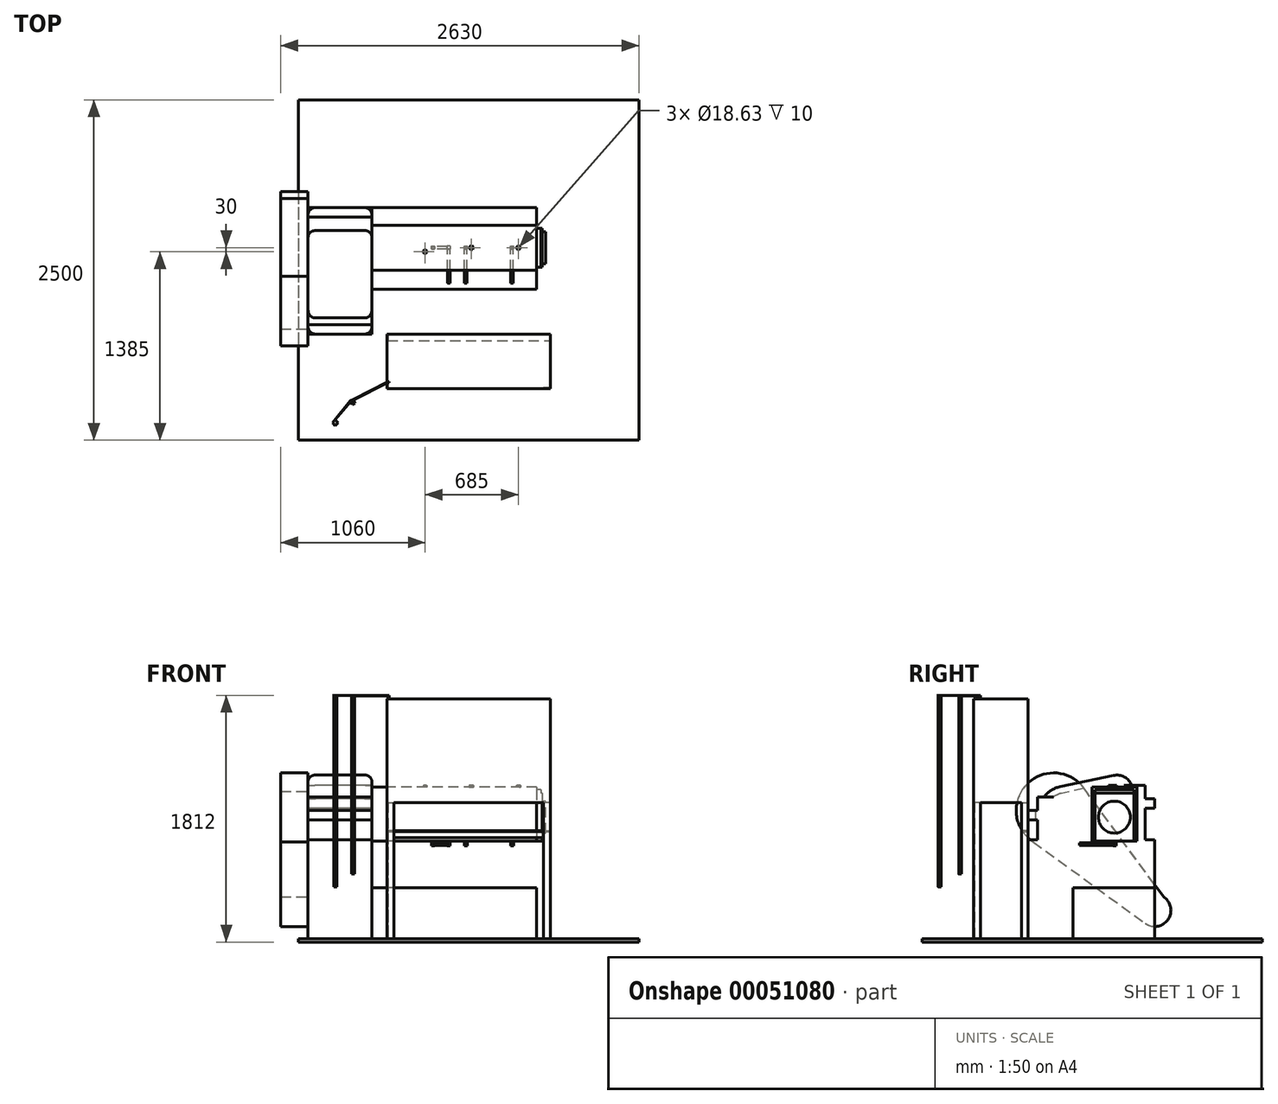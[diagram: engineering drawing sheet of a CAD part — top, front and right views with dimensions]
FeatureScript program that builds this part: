
annotation { "Feature Type Name" : "Feature", "Feature Type Description" : "" }
export const myFeature = defineFeature(function(context is Context, id is Id, definition is map)
    precondition{}
    {
        {
            var Q0;
            Q0=qCreatedBy(makeId("Top.planeOp"),FACE);
            var sketch = newSketch(context, id + "F0", { "sketchPlane" : qUnion([Q0])});
            skLineSegment(sketch, "E0.bottom", {"start": v(-1250, 1250) * mm, "end": v(1250, 1250) * mm});
            skLineSegment(sketch, "E0.top", {"start": v(-1250, -1250) * mm, "end": v(1250, -1250) * mm});
            skLineSegment(sketch, "E0.left", {"start": v(-1250, 1250) * mm, "end": v(-1250, -1250) * mm});
            skLineSegment(sketch, "E0.right", {"start": v(1250, 1250) * mm, "end": v(1250, -1250) * mm});
            skSolve(sketch);
        }
        {
            var Q0;
            Q0=qSketchRegion(id+"F0",true);
            extrude(context, id + "F1", {"entities" : qUnion([Q0]), "depth" : 25 * mm});
        }
        {
            var Q0;
            Q0=makeQuery(id+"F1.opExtrude","CAP_FACE",FACE,{"disambiguationData":[OSD([sQuery(id+"F0.wireOp",EDGE,"E0.bottom"),sQuery(id+"F0.wireOp",EDGE,"E0.top"),sQuery(id+"F0.wireOp",EDGE,"E0.left"),sQuery(id+"F0.wireOp",EDGE,"E0.right")])],"isStart":false});
            var sketch = newSketch(context, id + "F2", { "sketchPlane" : qUnion([Q0])});
            skLineSegment(sketch, "E1", {"start": v(-595, -520) * mm, "end": v(-595, -475) * mm});
            skLineSegment(sketch, "E2", {"start": v(-595, -475) * mm, "end": v(-550, -475) * mm});
            skLineSegment(sketch, "E3", {"start": v(-550, -475) * mm, "end": v(-550, -470) * mm});
            skLineSegment(sketch, "E4", {"start": v(-550, -470) * mm, "end": v(-600, -470) * mm});
            skLineSegment(sketch, "E5", {"start": v(-600, -470) * mm, "end": v(-600, -520) * mm});
            skLineSegment(sketch, "E6", {"start": v(-600, -520) * mm, "end": v(-595, -520) * mm});
            skLineSegment(sketch, "E7.MirrorCS", {"start": v(600, -520) * mm, "end": v(595, -520) * mm});
            skLineSegment(sketch, "E8.MirrorCS", {"start": v(550, -475) * mm, "end": v(550, -470) * mm});
            skLineSegment(sketch, "E9.MirrorCS", {"start": v(600, -470) * mm, "end": v(600, -520) * mm});
            skLineSegment(sketch, "E10.MirrorCS", {"start": v(550, -470) * mm, "end": v(600, -470) * mm});
            skLineSegment(sketch, "E11.MirrorCS", {"start": v(595, -475) * mm, "end": v(550, -475) * mm});
            skLineSegment(sketch, "E12.MirrorCS", {"start": v(595, -520) * mm, "end": v(595, -475) * mm});
            skLineSegment(sketch, "E13", {"start": v(-600, -820) * mm, "end": v(-595, -820) * mm});
            skLineSegment(sketch, "E14", {"start": v(-595, -820) * mm, "end": v(-595, -865) * mm});
            skLineSegment(sketch, "E15", {"start": v(-595, -865) * mm, "end": v(-550, -865) * mm});
            skLineSegment(sketch, "E16", {"start": v(-550, -865) * mm, "end": v(-550, -870) * mm});
            skLineSegment(sketch, "E17", {"start": v(-550, -870) * mm, "end": v(-600, -870) * mm});
            skLineSegment(sketch, "E18", {"start": v(-600, -870) * mm, "end": v(-600, -820) * mm});
            skLineSegment(sketch, "E19.MirrorCS", {"start": v(600, -820) * mm, "end": v(595, -820) * mm});
            skLineSegment(sketch, "E20.MirrorCS", {"start": v(550, -865) * mm, "end": v(550, -870) * mm});
            skLineSegment(sketch, "E21.MirrorCS", {"start": v(595, -820) * mm, "end": v(595, -865) * mm});
            skLineSegment(sketch, "E22.MirrorCS", {"start": v(550, -870) * mm, "end": v(600, -870) * mm});
            skLineSegment(sketch, "E23.MirrorCS", {"start": v(600, -870) * mm, "end": v(600, -820) * mm});
            skLineSegment(sketch, "E24.MirrorCS", {"start": v(595, -865) * mm, "end": v(550, -865) * mm});
            skSolve(sketch);
        }
        {
            var Q0;
            Q0=qSketchRegion(id+"F2",true);
            extrude(context, id + "F3", {"entities" : qUnion([Q0]), "operationType" : NewBodyOperationType.ADD, "depth" : 1000 * mm});
        }
        {
            var Q0;
            Q0=makeQuery(id+"F3.opExtrude","CAP_FACE",FACE,{"disambiguationData":[OSD([sQuery(id+"F2.wireOp",EDGE,"E7.MirrorCS"),sQuery(id+"F2.wireOp",EDGE,"E8.MirrorCS"),sQuery(id+"F2.wireOp",EDGE,"E9.MirrorCS"),sQuery(id+"F2.wireOp",EDGE,"E10.MirrorCS"),sQuery(id+"F2.wireOp",EDGE,"E11.MirrorCS"),sQuery(id+"F2.wireOp",EDGE,"E12.MirrorCS")])],"isStart":false});
            var sketch = newSketch(context, id + "F4", { "sketchPlane" : qUnion([Q0])});
            skLineSegment(sketch, "E25.bottom", {"start": v(600, -470) * mm, "end": v(-600, -470) * mm});
            skLineSegment(sketch, "E25.top", {"start": v(600, -870) * mm, "end": v(-600, -870) * mm});
            skLineSegment(sketch, "E25.left", {"start": v(600, -470) * mm, "end": v(600, -870) * mm});
            skLineSegment(sketch, "E25.right", {"start": v(-600, -470) * mm, "end": v(-600, -870) * mm});
            skSolve(sketch);
        }
        {
            var Q0;
            Q0=qSketchRegion(id+"F4",true);
            extrude(context, id + "F5", {"entities" : qUnion([Q0]), "operationType" : NewBodyOperationType.ADD, "depth" : 760 * mm});
        }
        {
            var Q0;
            Q0=makeQuery(id+"F1.opExtrude","CAP_FACE",FACE,{"disambiguationData":[OSD([sQuery(id+"F0.wireOp",EDGE,"E0.bottom"),sQuery(id+"F0.wireOp",EDGE,"E0.top"),sQuery(id+"F0.wireOp",EDGE,"E0.left"),sQuery(id+"F0.wireOp",EDGE,"E0.right")])],"isStart":false});
            var sketch = newSketch(context, id + "F6", { "sketchPlane" : qUnion([Q0])});
            skLineSegment(sketch, "E26.bottom", {"start": v(500, -140) * mm, "end": v(-710, -140) * mm});
            skLineSegment(sketch, "E26.top", {"start": v(500, 460) * mm, "end": v(-710, 460) * mm});
            skLineSegment(sketch, "E26.left", {"start": v(500, -140) * mm, "end": v(500, 460) * mm});
            skLineSegment(sketch, "E26.right", {"start": v(-710, -140) * mm, "end": v(-710, 460) * mm});
            skSolve(sketch);
        }
        {
            var Q0;
            Q0=qSketchRegion(id+"F6",true);
            extrude(context, id + "F7", {"entities" : qUnion([Q0]), "operationType" : NewBodyOperationType.ADD, "depth" : (1125 - 750) * mm});
        }
        {
            var Q0;
            Q0=makeQuery(id+"F1.opExtrude","CAP_FACE",FACE,{"disambiguationData":[OSD([sQuery(id+"F0.wireOp",EDGE,"E0.bottom"),sQuery(id+"F0.wireOp",EDGE,"E0.top"),sQuery(id+"F0.wireOp",EDGE,"E0.left"),sQuery(id+"F0.wireOp",EDGE,"E0.right")])],"isStart":false});
            var sketch = newSketch(context, id + "F8", { "sketchPlane" : qUnion([Q0])});
            skLineSegment(sketch, "E27.bottom", {"start": v(-710, -470) * mm, "end": v(-1180, -470) * mm});
            skLineSegment(sketch, "E27.top", {"start": v(-710, 460) * mm, "end": v(-1180, 460) * mm});
            skLineSegment(sketch, "E27.left", {"start": v(-710, -470) * mm, "end": v(-710, 460) * mm});
            skLineSegment(sketch, "E27.right", {"start": v(-1180, -470) * mm, "end": v(-1180, 460) * mm});
            skSolve(sketch);
        }
        {
            var Q0;
            Q0=qSketchRegion(id+"F8",true);
            extrude(context, id + "F9", {"entities" : qUnion([Q0]), "operationType" : NewBodyOperationType.ADD, "depth" : 727 * mm});
        }
        {
            var Q0;
            Q0=makeQuery(id+"F5.opExtrude","CAP_FACE",FACE,{"disambiguationData":[OSD([sQuery(id+"F4.wireOp",EDGE,"E25.bottom"),sQuery(id+"F4.wireOp",EDGE,"E25.top"),sQuery(id+"F4.wireOp",EDGE,"E25.left"),sQuery(id+"F4.wireOp",EDGE,"E25.right")])],"isStart":false});
            var sketch = newSketch(context, id + "F10", { "sketchPlane" : qUnion([Q0])});
            skCircle(sketch, "E28", {"center": v(-980, -1120) * mm, "radius": 10.48 * mm});
            skSolve(sketch);
        }
        {
            var Q0;
            Q0=makeQuery(id+"F10.imprint","IMPRINT",FACE,{"disambiguationData":[TD([[makeQuery(id+"F10.imprint","IMPRINT",EDGE,{"derivedFrom":makeQuery(id+"F5.opExtrude","CAP_EDGE",EDGE,{"disambiguationData":[OSD([sQuery(id+"F4.wireOp",EDGE,"E25.bottom")])],"isStart":false})}),1.0]])]});
            var sketch = newSketch(context, id + "F11", { "sketchPlane" : qUnion([Q0])});
            skLineSegment(sketch, "E29.bottom", {"start": v(-594.03, -820.45) * mm, "end": v(-583.06, -820.45) * mm});
            skLineSegment(sketch, "E29.top", {"start": v(-594.03, -827.38) * mm, "end": v(-583.06, -827.38) * mm});
            skLineSegment(sketch, "E29.left", {"start": v(-594.03, -820.45) * mm, "end": v(-594.03, -827.38) * mm});
            skLineSegment(sketch, "E29.right", {"start": v(-583.06, -820.45) * mm, "end": v(-583.06, -827.38) * mm});
            skSolve(sketch);
        }
        {
            var Q0;
            Q0=qSketchRegion(id+"F11",true);
            extrude(context, id + "F12", {"entities" : qUnion([Q0]), "operationType" : NewBodyOperationType.ADD, "depth" : 25 * mm});
        }
        {
            var Q0;
            Q0=makeQuery(id+"F12.opExtrude","CAP_FACE",FACE,{"disambiguationData":[OSD([sQuery(id+"F11.wireOp",EDGE,"E29.bottom"),sQuery(id+"F11.wireOp",EDGE,"E29.top"),sQuery(id+"F11.wireOp",EDGE,"E29.left"),sQuery(id+"F11.wireOp",EDGE,"E29.right")])],"isStart":false});
            var sketch = newSketch(context, id + "F13", { "sketchPlane" : qUnion([Q0])});
            skLineSegment(sketch, "E30", {"start": v(-583.06, -820.45) * mm, "end": v(-594.03, -820.45) * mm});
            skLineSegment(sketch, "E31", {"start": v(-594.03, -820.45) * mm, "end": v(-868.38, -960.9) * mm});
            skLineSegment(sketch, "E32", {"start": v(-868.38, -960.9) * mm, "end": v(-853.9, -989.2) * mm});
            skLineSegment(sketch, "E33", {"start": v(-853.9, -989.2) * mm, "end": v(-833.38, -978.7) * mm});
            skLineSegment(sketch, "E34", {"start": v(-833.38, -978.7) * mm, "end": v(-843.32, -953.7) * mm});
            skLineSegment(sketch, "E35", {"start": v(-843.32, -953.7) * mm, "end": v(-594.03, -827.38) * mm});
            skLineSegment(sketch, "E36", {"start": v(-594.03, -827.38) * mm, "end": v(-583.06, -827.38) * mm});
            skLineSegment(sketch, "E37", {"start": v(-583.06, -827.38) * mm, "end": v(-583.06, -820.45) * mm});
            skSolve(sketch);
        }
        {
            var Q0;
            Q0=qSketchRegion(id+"F13",true);
            extrude(context, id + "F14", {"entities" : qUnion([Q0]), "operationType" : NewBodyOperationType.ADD, "depth" : 1 * mm});
        }
        {
            var Q0;
            Q0=makeQuery(id+"F14.opExtrude","CAP_FACE",FACE,{"disambiguationData":[OSD([sQuery(id+"F13.wireOp",EDGE,"E30"),sQuery(id+"F13.wireOp",EDGE,"E31"),sQuery(id+"F13.wireOp",EDGE,"E32"),sQuery(id+"F13.wireOp",EDGE,"E33"),sQuery(id+"F13.wireOp",EDGE,"E34"),sQuery(id+"F13.wireOp",EDGE,"E35"),sQuery(id+"F13.wireOp",EDGE,"E36"),sQuery(id+"F13.wireOp",EDGE,"E37")])],"isStart":false});
            var sketch = newSketch(context, id + "F15", { "sketchPlane" : qUnion([Q0])});
            skLineSegment(sketch, "E38", {"start": v(-868.38, -960.9) * mm, "end": v(-1001.05, -1121.74) * mm});
            skLineSegment(sketch, "E39", {"start": v(-1001.05, -1121.74) * mm, "end": v(-979.08, -1142.68) * mm});
            skLineSegment(sketch, "E40", {"start": v(-979.08, -1142.68) * mm, "end": v(-959.11, -1121.73) * mm});
            skLineSegment(sketch, "E41", {"start": v(-959.11, -1121.73) * mm, "end": v(-979.08, -1100.8) * mm});
            skLineSegment(sketch, "E42", {"start": v(-979.08, -1100.8) * mm, "end": v(-865.6, -966.33) * mm});
            skLineSegment(sketch, "E43", {"start": v(-865.6, -966.33) * mm, "end": v(-853.9, -989.2) * mm});
            skLineSegment(sketch, "E44", {"start": v(-853.9, -989.2) * mm, "end": v(-833.38, -978.7) * mm});
            skLineSegment(sketch, "E45", {"start": v(-833.38, -978.7) * mm, "end": v(-847.86, -950.4) * mm});
            skLineSegment(sketch, "E46", {"start": v(-847.86, -950.4) * mm, "end": v(-868.38, -960.9) * mm});
            skSolve(sketch);
        }
        {
            var Q0;
            Q0=qSketchRegion(id+"F15",true);
            extrude(context, id + "F16", {"entities" : qUnion([Q0]), "operationType" : NewBodyOperationType.ADD, "depth" : 1 * mm});
        }
        {
            var Q0;
            Q0=makeQuery(id+"F14.opExtrude","CAP_FACE",FACE,{"disambiguationData":[OSD([sQuery(id+"F13.wireOp",EDGE,"E30"),sQuery(id+"F13.wireOp",EDGE,"E31"),sQuery(id+"F13.wireOp",EDGE,"E32"),sQuery(id+"F13.wireOp",EDGE,"E33"),sQuery(id+"F13.wireOp",EDGE,"E34"),sQuery(id+"F13.wireOp",EDGE,"E35"),sQuery(id+"F13.wireOp",EDGE,"E36"),sQuery(id+"F13.wireOp",EDGE,"E37")])],"isStart":true});
            var sketch = newSketch(context, id + "F17", { "sketchPlane" : qUnion([Q0])});
            skCircle(sketch, "E47", {"center": v(-850, 970) * mm, "radius": 10.48 * mm});
            skSolve(sketch);
        }
        {
            var Q0;
            Q0=qSketchRegion(id+"F17",true);
            extrude(context, id + "F18", {"entities" : qUnion([Q0]), "operationType" : NewBodyOperationType.ADD, "depth" : 1310 * mm});
        }
        {
            var Q0;
            Q0=makeQuery(id+"F16.opExtrude","CAP_FACE",FACE,{"disambiguationData":[OSD([sQuery(id+"F15.wireOp",EDGE,"E38"),sQuery(id+"F15.wireOp",EDGE,"E39"),sQuery(id+"F15.wireOp",EDGE,"E40"),sQuery(id+"F15.wireOp",EDGE,"E41"),sQuery(id+"F15.wireOp",EDGE,"E42"),sQuery(id+"F15.wireOp",EDGE,"E43"),sQuery(id+"F15.wireOp",EDGE,"E44"),sQuery(id+"F15.wireOp",EDGE,"E45"),sQuery(id+"F15.wireOp",EDGE,"E46")])],"isStart":true});
            var sketch = newSketch(context, id + "F19", { "sketchPlane" : qUnion([Q0])});
            skCircle(sketch, "E48", {"center": v(-980, 1120) * mm, "radius": 10.48 * mm});
            skSolve(sketch);
        }
        {
            var Q0;
            Q0=qSketchRegion(id+"F19",true);
            extrude(context, id + "F20", {"entities" : qUnion([Q0]), "operationType" : NewBodyOperationType.ADD, "depth" : 1406.4 * mm});
        }
        {
            var Q0;
            Q0=makeQuery(id+"F9.opExtrude","SWEPT_FACE",FACE,{"disambiguationData":[OSD([sQuery(id+"F8.wireOp",EDGE,"E27.right")])]});
            var sketch = newSketch(context, id + "F21", { "sketchPlane" : qUnion([Q0])});
            skLineSegment(sketch, "E49.bottom", {"start": v(400, 675.87) * mm, "end": v(-390, 675.87) * mm});
            skLineSegment(sketch, "E50", {"start": v(-390, 675.87) * mm, "end": v(-390, 982) * mm});
            skLineSegment(sketch, "E51", {"start": v(-390, 982) * mm, "end": v(-460, 982) * mm});
            skLineSegment(sketch, "E52", {"start": v(-460, 982) * mm, "end": v(-460, 1052) * mm});
            skLineSegment(sketch, "E53", {"start": v(-460, 1052) * mm, "end": v(-390, 1052) * mm});
            skLineSegment(sketch, "E54", {"start": v(-390, 1052) * mm, "end": v(-390, 1152) * mm});
            skLineSegment(sketch, "E55", {"start": v(-390, 1152) * mm, "end": v(-290, 1152) * mm});
            skLineSegment(sketch, "E56", {"start": v(-290, 1152) * mm, "end": v(-290, 1252) * mm});
            skLineSegment(sketch, "E57", {"start": v(400, 675.87) * mm, "end": v(400, 897) * mm});
            skLineSegment(sketch, "E58", {"start": v(400, 897) * mm, "end": v(470, 897) * mm});
            skLineSegment(sketch, "E59", {"start": v(470, 897) * mm, "end": v(470, 967) * mm});
            skLineSegment(sketch, "E60", {"start": v(470, 967) * mm, "end": v(400, 967) * mm});
            skLineSegment(sketch, "E61", {"start": v(400, 967) * mm, "end": v(400, 1067) * mm});
            skLineSegment(sketch, "E62", {"start": v(400, 1067) * mm, "end": v(351.87, 1067) * mm});
            skLineSegment(sketch, "E63", {"start": v(351.87, 1067) * mm, "end": v(351.87, 1117) * mm});
            skLineSegment(sketch, "E64", {"start": v(-290, 1252) * mm, "end": v(351.87, 1117) * mm});
            skSolve(sketch);
        }
        {
            var Q0;
            Q0=qSketchRegion(id+"F21",true);
            extrude(context, id + "F22", {"entities" : qUnion([Q0]), "operationType" : NewBodyOperationType.ADD, "oppositeDirection" : true, "depth" : 470 * mm});
        }
        {
            var Q0;
            Q0=makeQuery(id+"F22.opExtrude","SWEPT_EDGE",EDGE,{"disambiguationData":[OSD([sQuery(id+"F21.wireOp",EDGE,"E56"),sQuery(id+"F21.wireOp",EDGE,"E64")])]});
            fillet(context, id + "F23", {"entities" : qUnion([Q0]), "radius" : 116.8 * mm, "tangentPropagation" : true, "allowEdgeOverflow" : false});
        }
        {
            var Q0;
            Q0=makeQuery(id+"F22.opExtrude","SWEPT_EDGE",EDGE,{"disambiguationData":[OSD([sQuery(id+"F21.wireOp",EDGE,"E63"),sQuery(id+"F21.wireOp",EDGE,"E64")])]});
            fillet(context, id + "F24", {"entities" : qUnion([Q0]), "radius" : 190.82 * mm, "tangentPropagation" : true, "allowEdgeOverflow" : false});
        }
        {
            var Q0;
            Q0=makeQuery(id+"F22.opExtrude","CAP_EDGE",EDGE,{"disambiguationData":[OSD([sQuery(id+"F21.wireOp",EDGE,"E64")])],"isStart":false});
            var Q1;
            Q1=makeQuery(id+"F22.opExtrude","CAP_EDGE",EDGE,{"disambiguationData":[OSD([sQuery(id+"F21.wireOp",EDGE,"E64")])],"isStart":true});
            fillet(context, id + "F25", {"entities" : qUnion([Q0, Q1]), "radius" : 50 * mm, "tangentPropagation" : true, "allowEdgeOverflow" : false});
        }
        {
            var Q0;
            Q0=makeQuery(id+"F22.opExtrude","CAP_EDGE",EDGE,{"disambiguationData":[OSD([sQuery(id+"F21.wireOp",EDGE,"E52")])],"isStart":false});
            var Q1;
            Q1=makeQuery(id+"F22.opExtrude","CAP_EDGE",EDGE,{"disambiguationData":[OSD([sQuery(id+"F21.wireOp",EDGE,"E52")])],"isStart":true});
            var Q2;
            Q2=makeQuery(id+"F22.opExtrude","CAP_EDGE",EDGE,{"disambiguationData":[OSD([sQuery(id+"F21.wireOp",EDGE,"E59")])],"isStart":true});
            var Q3;
            Q3=makeQuery(id+"F22.opExtrude","CAP_EDGE",EDGE,{"disambiguationData":[OSD([sQuery(id+"F21.wireOp",EDGE,"E59")])],"isStart":false});
            fillet(context, id + "F26", {"entities" : qUnion([Q0, Q1, Q2, Q3]), "radius" : 55 * mm, "tangentPropagation" : true, "allowEdgeOverflow" : false});
        }
        {
            var Q0;
            Q0=makeQuery(id+"F22.boolean.opBoolean","MERGE",FACE,{"derivedFrom":[makeQuery(id+"F9.opExtrude","SWEPT_FACE",FACE,{"disambiguationData":[OSD([sQuery(id+"F8.wireOp",EDGE,"E27.left")])]}),makeQuery(id+"F22.opExtrude","CAP_FACE",FACE,{"disambiguationData":[OSD([sQuery(id+"F21.wireOp",EDGE,"E49.bottom"),sQuery(id+"F21.wireOp",EDGE,"E50"),sQuery(id+"F21.wireOp",EDGE,"E51"),sQuery(id+"F21.wireOp",EDGE,"E52"),sQuery(id+"F21.wireOp",EDGE,"E53"),sQuery(id+"F21.wireOp",EDGE,"E54"),sQuery(id+"F21.wireOp",EDGE,"E55"),sQuery(id+"F21.wireOp",EDGE,"E56"),sQuery(id+"F21.wireOp",EDGE,"E57"),sQuery(id+"F21.wireOp",EDGE,"E58"),sQuery(id+"F21.wireOp",EDGE,"E59"),sQuery(id+"F21.wireOp",EDGE,"E60"),sQuery(id+"F21.wireOp",EDGE,"E61"),sQuery(id+"F21.wireOp",EDGE,"E62"),sQuery(id+"F21.wireOp",EDGE,"E63"),sQuery(id+"F21.wireOp",EDGE,"E64")])],"isStart":false})]});
            var sketch = newSketch(context, id + "F27", { "sketchPlane" : qUnion([Q0])});
            skLineSegment(sketch, "E65.bottom", {"start": v(0, 1140) * mm, "end": v(330, 1140) * mm});
            skLineSegment(sketch, "E65.top", {"start": v(0, 743) * mm, "end": v(330, 743) * mm});
            skLineSegment(sketch, "E65.left", {"start": v(0, 1140) * mm, "end": v(0, 743) * mm});
            skLineSegment(sketch, "E65.right", {"start": v(330, 1140) * mm, "end": v(330, 743) * mm});
            skSolve(sketch);
        }
        {
            var Q0;
            Q0=qSketchRegion(id+"F27",true);
            extrude(context, id + "F28", {"entities" : qUnion([Q0]), "operationType" : NewBodyOperationType.ADD, "depth" : 1210 * mm});
        }
        {
            var Q0;
            Q0=makeQuery(id+"F28.opExtrude","CAP_FACE",FACE,{"disambiguationData":[OSD([sQuery(id+"F27.wireOp",EDGE,"E65.bottom"),sQuery(id+"F27.wireOp",EDGE,"E65.top"),sQuery(id+"F27.wireOp",EDGE,"E65.left"),sQuery(id+"F27.wireOp",EDGE,"E65.right")])],"isStart":false});
            var sketch = newSketch(context, id + "F29", { "sketchPlane" : qUnion([Q0])});
            skLineSegment(sketch, "E66.bottom", {"start": v(22, 1118) * mm, "end": v(308, 1118) * mm});
            skLineSegment(sketch, "E66.top", {"start": v(22, 743) * mm, "end": v(308, 743) * mm});
            skLineSegment(sketch, "E66.left", {"start": v(22, 1118) * mm, "end": v(22, 743) * mm});
            skLineSegment(sketch, "E66.right", {"start": v(308, 1118) * mm, "end": v(308, 743) * mm});
            skSolve(sketch);
        }
        {
            var Q0;
            Q0=qSketchRegion(id+"F29",true);
            extrude(context, id + "F30", {"entities" : qUnion([Q0]), "operationType" : NewBodyOperationType.ADD, "depth" : 30 * mm});
        }
        {
            var Q0;
            Q0=makeQuery(id+"F30.opExtrude","CAP_FACE",FACE,{"disambiguationData":[OSD([sQuery(id+"F29.wireOp",EDGE,"E66.bottom"),sQuery(id+"F29.wireOp",EDGE,"E66.top"),sQuery(id+"F29.wireOp",EDGE,"E66.left"),sQuery(id+"F29.wireOp",EDGE,"E66.right")])],"isStart":false});
            var sketch = newSketch(context, id + "F31", { "sketchPlane" : qUnion([Q0])});
            skLineSegment(sketch, "E67.bottom", {"start": v(22, 743) * mm, "end": v(308, 743) * mm});
            skLineSegment(sketch, "E67.top", {"start": v(22, 1093) * mm, "end": v(308, 1093) * mm});
            skLineSegment(sketch, "E67.left", {"start": v(22, 743) * mm, "end": v(22, 1093) * mm});
            skLineSegment(sketch, "E67.right", {"start": v(308, 743) * mm, "end": v(308, 1093) * mm});
            skSolve(sketch);
        }
        {
            var Q0;
            Q0=qSketchRegion(id+"F31",true);
            extrude(context, id + "F32", {"entities" : qUnion([Q0]), "operationType" : NewBodyOperationType.ADD, "depth" : 9 * mm});
        }
        {
            var Q0;
            Q0=makeQuery(id+"F32.opExtrude","CAP_FACE",FACE,{"disambiguationData":[OSD([sQuery(id+"F31.wireOp",EDGE,"E67.bottom"),sQuery(id+"F31.wireOp",EDGE,"E67.top"),sQuery(id+"F31.wireOp",EDGE,"E67.left"),sQuery(id+"F31.wireOp",EDGE,"E67.right")])],"isStart":false});
            var sketch = newSketch(context, id + "F33", { "sketchPlane" : qUnion([Q0])});
            skCircle(sketch, "E68", {"center": v(163.06, 917.73) * mm, "radius": 117.5 * mm});
            skSolve(sketch);
        }
        {
            var Q0;
            Q0=qSketchRegion(id+"F33",true);
            extrude(context, id + "F34", {"entities" : qUnion([Q0]), "operationType" : NewBodyOperationType.ADD, "depth" : 25 * mm});
        }
        {
            var Q0;
            Q0=makeQuery(id+"F5.boolean.opBoolean","MERGE",FACE,{"derivedFrom":[makeQuery(id+"F3.opExtrude","SWEPT_FACE",FACE,{"disambiguationData":[OSD([sQuery(id+"F2.wireOp",EDGE,"E9.MirrorCS")])]}),makeQuery(id+"F3.opExtrude","SWEPT_FACE",FACE,{"disambiguationData":[OSD([sQuery(id+"F2.wireOp",EDGE,"E23.MirrorCS")])]}),makeQuery(id+"F5.opExtrude","SWEPT_FACE",FACE,{"disambiguationData":[OSD([sQuery(id+"F4.wireOp",EDGE,"E25.left")])]})]});
            var sketch = newSketch(context, id + "F35", { "sketchPlane" : qUnion([Q0])});
            skLineSegment(sketch, "E69", {"start": v(-520, 818) * mm, "end": v(-470, 818) * mm});
            skLineSegment(sketch, "E70", {"start": v(-470, 818) * mm, "end": v(-470, 768) * mm});
            skLineSegment(sketch, "E71", {"start": v(-470, 768) * mm, "end": v(-475, 768) * mm});
            skLineSegment(sketch, "E72", {"start": v(-475, 768) * mm, "end": v(-475, 813) * mm});
            skLineSegment(sketch, "E73", {"start": v(-475, 813) * mm, "end": v(-520, 813) * mm});
            skLineSegment(sketch, "E74", {"start": v(-520, 813) * mm, "end": v(-520, 818) * mm});
            skSolve(sketch);
        }
        {
            var Q0;
            Q0=qSketchRegion(id+"F35",true);
            extrude(context, id + "F36", {"entities" : qUnion([Q0]), "operationType" : NewBodyOperationType.ADD, "oppositeDirection" : true, "depth" : 1200 * mm});
        }
        {
            var Q0;
            Q0=makeQuery(id+"F28.opExtrude","SWEPT_FACE",FACE,{"disambiguationData":[OSD([sQuery(id+"F27.wireOp",EDGE,"E65.bottom")])]});
            var sketch = newSketch(context, id + "F37", { "sketchPlane" : qUnion([Q0])});
            skCircle(sketch, "E75.cCircle", {"center": v(365, 165) * mm, "radius": 13 * mm, "construction": true});
            skPoint(sketch, "E75.cCircle.centerSnap0", {"position": v(500, 165) * mm});
            skLineSegment(sketch, "E75.0", {"start": v(372.5, 152) * mm, "end": v(357.5, 152) * mm});
            skLineSegment(sketch, "E75.1", {"start": v(357.5, 152) * mm, "end": v(349.99, 165) * mm});
            skLineSegment(sketch, "E75.2", {"start": v(349.99, 165) * mm, "end": v(357.5, 178) * mm});
            skLineSegment(sketch, "E75.3", {"start": v(357.5, 178) * mm, "end": v(372.5, 178) * mm});
            skLineSegment(sketch, "E75.4", {"start": v(372.5, 178) * mm, "end": v(380.01, 165) * mm});
            skLineSegment(sketch, "E75.5", {"start": v(380.01, 165) * mm, "end": v(372.5, 152) * mm});
            skPoint(sketch, "E75.0.midPoint", {"position": v(365, 152) * mm});
            skCircle(sketch, "E76", {"center": v(365, 165) * mm, "radius": 9.32 * mm});
            skSolve(sketch);
        }
        {
            var Q0;
            Q0=qSketchRegion(id+"F37",true);
            extrude(context, id + "F38", {"entities" : qUnion([Q0]), "operationType" : NewBodyOperationType.ADD, "depth" : 10 * mm});
        }
        {
            var Q0;
            {var subQ0=sQuery(id+"F27.wireOp",EDGE,"E65.bottom");Q0=makeQuery(id+"F38.boolean.opBoolean","SPLIT",FACE,{"disambiguationData":[TD([makeQuery(id+"F9.opExtrude","SWEPT_FACE",FACE,{"disambiguationData":[OSD([sQuery(id+"F8.wireOp",EDGE,"E27.left")])]})])],"derivedFrom":makeQuery(id+"F28.opExtrude","SWEPT_FACE",FACE,{"disambiguationData":[OSD([subQ0])]})});}
            var sketch = newSketch(context, id + "F39", { "sketchPlane" : qUnion([Q0])});
            skCircle(sketch, "E77", {"center": v(20, 165) * mm, "radius": 9.32 * mm});
            skCircle(sketch, "E78.cCircle", {"center": v(20, 165) * mm, "radius": 13 * mm, "construction": true});
            skLineSegment(sketch, "E78.0", {"start": v(34.98, 165.9) * mm, "end": v(28.27, 152.47) * mm});
            skLineSegment(sketch, "E78.1", {"start": v(28.27, 152.47) * mm, "end": v(13.29, 151.57) * mm});
            skLineSegment(sketch, "E78.2", {"start": v(13.29, 151.57) * mm, "end": v(5.02, 164.1) * mm});
            skLineSegment(sketch, "E78.3", {"start": v(5.02, 164.1) * mm, "end": v(11.73, 177.53) * mm});
            skLineSegment(sketch, "E78.4", {"start": v(11.73, 177.53) * mm, "end": v(26.71, 178.43) * mm});
            skLineSegment(sketch, "E78.5", {"start": v(26.71, 178.43) * mm, "end": v(34.98, 165.9) * mm});
            skPoint(sketch, "E78.0.midPoint", {"position": v(31.63, 159.19) * mm});
            skSolve(sketch);
        }
        {
            var Q0;
            Q0=qSketchRegion(id+"F39",true);
            extrude(context, id + "F40", {"entities" : qUnion([Q0]), "operationType" : NewBodyOperationType.ADD, "depth" : 10 * mm});
        }
        {
            var Q0;
            {var subQ0=sQuery(id+"F27.wireOp",EDGE,"E65.bottom");var subQ9=makeQuery(id+"F9.opExtrude","SWEPT_FACE",FACE,{"disambiguationData":[OSD([sQuery(id+"F8.wireOp",EDGE,"E27.left")])]});Q0=makeQuery(id+"F40.boolean.opBoolean","SPLIT",FACE,{"disambiguationData":[TD([subQ9])],"derivedFrom":makeQuery(id+"F38.boolean.opBoolean","SPLIT",FACE,{"disambiguationData":[TD([subQ9])],"derivedFrom":makeQuery(id+"F28.opExtrude","SWEPT_FACE",FACE,{"disambiguationData":[OSD([subQ0])]})})});}
            var sketch = newSketch(context, id + "F41", { "sketchPlane" : qUnion([Q0])});
            skCircle(sketch, "E79", {"center": v(-320, 135) * mm, "radius": 9.32 * mm});
            skCircle(sketch, "E80.cCircle", {"center": v(-320, 135) * mm, "radius": 13 * mm, "construction": true});
            skLineSegment(sketch, "E80.0", {"start": v(-307, 142.5) * mm, "end": v(-307, 127.5) * mm});
            skLineSegment(sketch, "E80.1", {"start": v(-307, 127.5) * mm, "end": v(-320, 119.99) * mm});
            skLineSegment(sketch, "E80.2", {"start": v(-320, 119.99) * mm, "end": v(-333, 127.5) * mm});
            skLineSegment(sketch, "E80.3", {"start": v(-333, 127.5) * mm, "end": v(-333, 142.5) * mm});
            skLineSegment(sketch, "E80.4", {"start": v(-333, 142.5) * mm, "end": v(-320, 150.01) * mm});
            skLineSegment(sketch, "E80.5", {"start": v(-320, 150.01) * mm, "end": v(-307, 142.5) * mm});
            skPoint(sketch, "E80.0.midPoint", {"position": v(-307, 135) * mm});
            skSolve(sketch);
        }
        {
            var Q0;
            Q0=qSketchRegion(id+"F41",true);
            extrude(context, id + "F42", {"entities" : qUnion([Q0]), "operationType" : NewBodyOperationType.ADD, "depth" : 10 * mm});
        }
        {
            var Q0;
            Q0=makeQuery(id+"F32.boolean.opBoolean","MERGE",FACE,{"derivedFrom":[makeQuery(id+"F30.boolean.opBoolean","MERGE",FACE,{"derivedFrom":[makeQuery(id+"F28.opExtrude","SWEPT_FACE",FACE,{"disambiguationData":[OSD([sQuery(id+"F27.wireOp",EDGE,"E65.top")])]}),makeQuery(id+"F30.opExtrude","SWEPT_FACE",FACE,{"disambiguationData":[OSD([sQuery(id+"F29.wireOp",EDGE,"E66.top")])]})]}),makeQuery(id+"F32.opExtrude","SWEPT_FACE",FACE,{"disambiguationData":[OSD([sQuery(id+"F31.wireOp",EDGE,"E67.bottom")])]})]});
            var sketch = newSketch(context, id + "F43", { "sketchPlane" : qUnion([Q0])});
            skCircle(sketch, "E81", {"center": v(319, -165) * mm, "radius": 9.32 * mm});
            skCircle(sketch, "E82", {"center": v(-21, -165) * mm, "radius": 9.32 * mm});
            skCircle(sketch, "E83", {"center": v(-261, -165) * mm, "radius": 9.32 * mm});
            skSolve(sketch);
        }
        {
            var Q0;
            Q0=qSketchRegion(id+"F43",true);
            extrude(context, id + "F44", {"entities" : qUnion([Q0]), "operationType" : NewBodyOperationType.ADD, "depth" : 13 * mm});
        }
        {
            var Q0;
            Q0=makeQuery(id+"F44.opExtrude","CAP_FACE",FACE,{"disambiguationData":[OSD([sQuery(id+"F43.wireOp",EDGE,"E81")])],"isStart":false});
            var sketch = newSketch(context, id + "F45", { "sketchPlane" : qUnion([Q0])});
            skLineSegment(sketch, "E84.rect.bottom", {"start": v(308, -154) * mm, "end": v(330, -154) * mm});
            skLineSegment(sketch, "E84.rect.top", {"start": v(308, -176) * mm, "end": v(330, -176) * mm});
            skLineSegment(sketch, "E84.rect.left", {"start": v(308, -154) * mm, "end": v(308, -176) * mm});
            skLineSegment(sketch, "E84.rect.right", {"start": v(330, -154) * mm, "end": v(330, -176) * mm});
            skPoint(sketch, "E84.rect.middle", {"position": v(319, -165) * mm});
            skSolve(sketch);
        }
        {
            var Q0;
            Q0=qSketchRegion(id+"F45",true);
            extrude(context, id + "F46", {"entities" : qUnion([Q0]), "operationType" : NewBodyOperationType.ADD, "depth" : 22 * mm});
        }
        {
            var Q0;
            Q0=makeQuery(id+"F44.opExtrude","CAP_FACE",FACE,{"disambiguationData":[OSD([sQuery(id+"F43.wireOp",EDGE,"E82")])],"isStart":false});
            var sketch = newSketch(context, id + "F47", { "sketchPlane" : qUnion([Q0])});
            skLineSegment(sketch, "E85.rect.bottom", {"start": v(-32, -154) * mm, "end": v(-10, -154) * mm});
            skLineSegment(sketch, "E85.rect.top", {"start": v(-32, -176) * mm, "end": v(-10, -176) * mm});
            skLineSegment(sketch, "E85.rect.left", {"start": v(-32, -154) * mm, "end": v(-32, -176) * mm});
            skLineSegment(sketch, "E85.rect.right", {"start": v(-10, -154) * mm, "end": v(-10, -176) * mm});
            skPoint(sketch, "E85.rect.middle", {"position": v(-21, -165) * mm});
            skSolve(sketch);
        }
        {
            var Q0;
            Q0=qSketchRegion(id+"F47",true);
            extrude(context, id + "F48", {"entities" : qUnion([Q0]), "operationType" : NewBodyOperationType.ADD, "depth" : 22 * mm});
        }
        {
            var Q0;
            Q0=makeQuery(id+"F44.opExtrude","CAP_FACE",FACE,{"disambiguationData":[OSD([sQuery(id+"F43.wireOp",EDGE,"E83")])],"isStart":false});
            var sketch = newSketch(context, id + "F49", { "sketchPlane" : qUnion([Q0])});
            skLineSegment(sketch, "E86.rect.bottom", {"start": v(-272, -154) * mm, "end": v(-250, -154) * mm});
            skLineSegment(sketch, "E86.rect.top", {"start": v(-272, -176) * mm, "end": v(-250, -176) * mm});
            skLineSegment(sketch, "E86.rect.left", {"start": v(-272, -154) * mm, "end": v(-272, -176) * mm});
            skLineSegment(sketch, "E86.rect.right", {"start": v(-250, -154) * mm, "end": v(-250, -176) * mm});
            skPoint(sketch, "E86.rect.middle", {"position": v(-261, -165) * mm});
            skSolve(sketch);
        }
        {
            var Q0;
            Q0=qSketchRegion(id+"F49",true);
            extrude(context, id + "F50", {"entities" : qUnion([Q0]), "operationType" : NewBodyOperationType.ADD, "depth" : 22 * mm});
        }
        {
            var Q0;
            Q0=makeQuery(id+"F48.opExtrude","SWEPT_FACE",FACE,{"disambiguationData":[OSD([sQuery(id+"F47.wireOp",EDGE,"E85.rect.bottom")])]});
            var sketch = newSketch(context, id + "F51", { "sketchPlane" : qUnion([Q0])});
            skCircle(sketch, "E87", {"center": v(-21, 719) * mm, "radius": 9.32 * mm});
            skSolve(sketch);
        }
        {
            var Q0;
            Q0=qSketchRegion(id+"F51",true);
            extrude(context, id + "F52", {"entities" : qUnion([Q0]), "operationType" : NewBodyOperationType.ADD, "depth" : 249 * mm});
        }
        {
            var Q0;
            Q0=makeQuery(id+"F46.opExtrude","SWEPT_FACE",FACE,{"disambiguationData":[OSD([sQuery(id+"F45.wireOp",EDGE,"E84.rect.bottom")])]});
            var sketch = newSketch(context, id + "F53", { "sketchPlane" : qUnion([Q0])});
            skCircle(sketch, "E88", {"center": v(319, 719) * mm, "radius": 9.32 * mm});
            skPoint(sketch, "E88.centerSnap0", {"position": v(330, 719) * mm});
            skPoint(sketch, "E88.centerSnap1", {"position": v(319, 730) * mm});
            skSolve(sketch);
        }
        {
            var Q0;
            Q0=qSketchRegion(id+"F53",true);
            extrude(context, id + "F54", {"entities" : qUnion([Q0]), "operationType" : NewBodyOperationType.ADD, "depth" : 249 * mm});
        }
        {
            var Q0;
            Q0=makeQuery(id+"F50.opExtrude","SWEPT_FACE",FACE,{"disambiguationData":[OSD([sQuery(id+"F49.wireOp",EDGE,"E86.rect.right")])]});
            var sketch = newSketch(context, id + "F55", { "sketchPlane" : qUnion([Q0])});
            skCircle(sketch, "E89", {"center": v(165, 719) * mm, "radius": 9.32 * mm});
            skPoint(sketch, "E89.centerSnap0", {"position": v(165, 730) * mm});
            skPoint(sketch, "E89.centerSnap1", {"position": v(176, 719) * mm});
            skSolve(sketch);
        }
        {
            var Q0;
            Q0=qSketchRegion(id+"F55",true);
            extrude(context, id + "F56", {"entities" : qUnion([Q0]), "operationType" : NewBodyOperationType.ADD, "depth" : (115 - 22) * mm});
        }
        {
            var Q0;
            Q0=makeQuery(id+"F56.opExtrude","CAP_FACE",FACE,{"disambiguationData":[OSD([sQuery(id+"F55.wireOp",EDGE,"E89")])],"isStart":false});
            var sketch = newSketch(context, id + "F57", { "sketchPlane" : qUnion([Q0])});
            skLineSegment(sketch, "E90.rect.bottom", {"start": v(176, 708) * mm, "end": v(154, 708) * mm});
            skLineSegment(sketch, "E90.rect.top", {"start": v(176, 730) * mm, "end": v(154, 730) * mm});
            skLineSegment(sketch, "E90.rect.left", {"start": v(176, 708) * mm, "end": v(176, 730) * mm});
            skLineSegment(sketch, "E90.rect.right", {"start": v(154, 708) * mm, "end": v(154, 730) * mm});
            skPoint(sketch, "E90.rect.middle", {"position": v(165, 719) * mm});
            skSolve(sketch);
        }
        {
            var Q0;
            Q0=qSketchRegion(id+"F57",true);
            extrude(context, id + "F58", {"entities" : qUnion([Q0]), "operationType" : NewBodyOperationType.ADD, "depth" : 22 * mm});
        }
        {
            var Q0;
            Q0=makeQuery(id+"F58.opExtrude","SWEPT_FACE",FACE,{"disambiguationData":[OSD([sQuery(id+"F57.wireOp",EDGE,"E90.rect.right")])]});
            var sketch = newSketch(context, id + "F59", { "sketchPlane" : qUnion([Q0])});
            skCircle(sketch, "E91", {"center": v(-146, 719) * mm, "radius": 9.32 * mm});
            skPoint(sketch, "E91.centerSnap0", {"position": v(-135, 719) * mm});
            skPoint(sketch, "E91.centerSnap1", {"position": v(-146, 730) * mm});
            skSolve(sketch);
        }
        {
            var Q0;
            Q0=qSketchRegion(id+"F59",true);
            extrude(context, id + "F60", {"entities" : qUnion([Q0]), "operationType" : NewBodyOperationType.ADD, "depth" : 249 * mm});
        }
        {
            var Q0;
            Q0=makeQuery(id+"F22.boolean.opBoolean","MERGE",FACE,{"derivedFrom":[makeQuery(id+"F9.opExtrude","SWEPT_FACE",FACE,{"disambiguationData":[OSD([sQuery(id+"F8.wireOp",EDGE,"E27.right")])]}),makeQuery(id+"F22.opExtrude","CAP_FACE",FACE,{"disambiguationData":[OSD([sQuery(id+"F21.wireOp",EDGE,"E49.bottom"),sQuery(id+"F21.wireOp",EDGE,"E50"),sQuery(id+"F21.wireOp",EDGE,"E51"),sQuery(id+"F21.wireOp",EDGE,"E52"),sQuery(id+"F21.wireOp",EDGE,"E53"),sQuery(id+"F21.wireOp",EDGE,"E54"),sQuery(id+"F21.wireOp",EDGE,"E55"),sQuery(id+"F21.wireOp",EDGE,"E56"),sQuery(id+"F21.wireOp",EDGE,"E57"),sQuery(id+"F21.wireOp",EDGE,"E58"),sQuery(id+"F21.wireOp",EDGE,"E59"),sQuery(id+"F21.wireOp",EDGE,"E60"),sQuery(id+"F21.wireOp",EDGE,"E61"),sQuery(id+"F21.wireOp",EDGE,"E62"),sQuery(id+"F21.wireOp",EDGE,"E63"),sQuery(id+"F21.wireOp",EDGE,"E64")])],"isStart":true})]});
            var sketch = newSketch(context, id + "F61", { "sketchPlane" : qUnion([Q0])});
            skCircle(sketch, "E92", {"center": v(282.39, 967) * mm, "radius": 275.74 * mm});
            skCircle(sketch, "E93", {"center": v(-460, 232.23) * mm, "radius": 118.14 * mm});
            skLineSegment(sketch, "E94", {"start": v(-525.3, 330.68) * mm, "end": v(78.82, 1152.98) * mm});
            skLineSegment(sketch, "E95", {"start": v(455.03, 752) * mm, "end": v(-390.49, 136.7) * mm});
            skSolve(sketch);
        }
        {
            var Q0;
            Q0=qSketchRegion(id+"F61",true);
            extrude(context, id + "F62", {"entities" : qUnion([Q0]), "operationType" : NewBodyOperationType.ADD, "depth" : 200 * mm});
        }
    });
